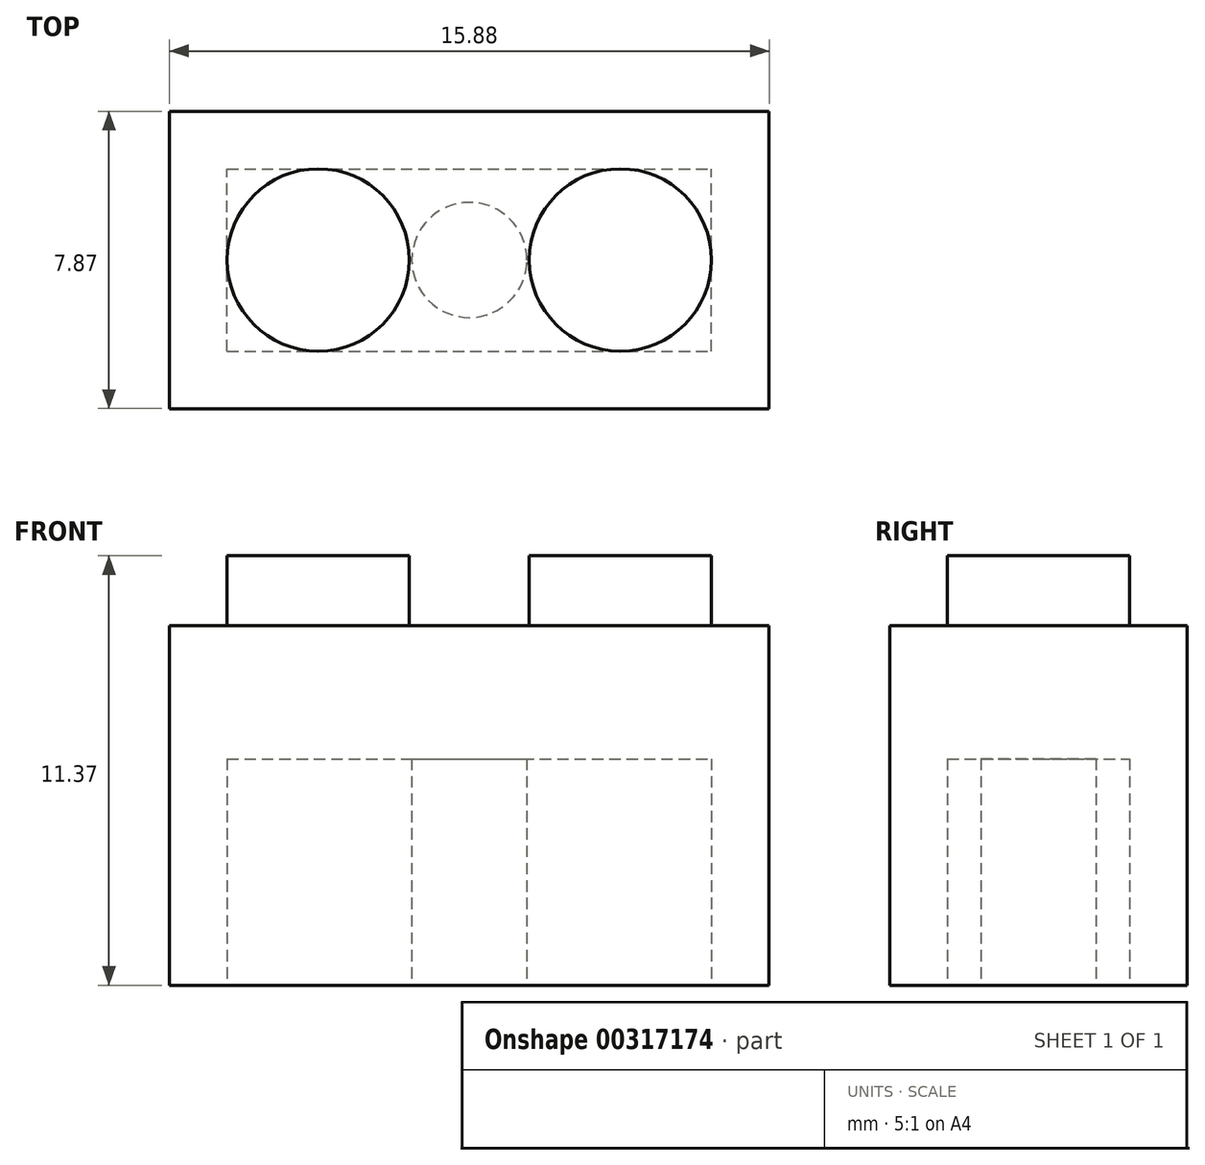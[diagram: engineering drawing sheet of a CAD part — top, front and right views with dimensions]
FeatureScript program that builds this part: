
annotation { "Feature Type Name" : "Feature", "Feature Type Description" : "" }
export const myFeature = defineFeature(function(context is Context, id is Id, definition is map)
    precondition{}
    {
        {
            var Q0;
            Q0=qCreatedBy(makeId("Front.planeOp"),FACE);
            var sketch = newSketch(context, id + "F0", { "sketchPlane" : qUnion([Q0])});
            skLineSegment(sketch, "E0.bottom", {"start": v(-8.22, 8.85) * mm, "end": v(7.66, 8.85) * mm});
            skLineSegment(sketch, "E0.top", {"start": v(-8.22, -0.67) * mm, "end": v(7.66, -0.67) * mm});
            skLineSegment(sketch, "E0.left", {"start": v(-8.22, 8.85) * mm, "end": v(-8.22, -0.67) * mm});
            skLineSegment(sketch, "E0.right", {"start": v(7.66, 8.85) * mm, "end": v(7.66, -0.67) * mm});
            skSolve(sketch);
        }
        {
            var Q0;
            Q0 = qSketchRegion(id + "F0", true);
            extrude(context, id + "F1", {"entities" : qUnion([Q0]), "depth" : 7.87 * mm});
        }
        {
            var Q0;
            Q0=makeQuery(id+"F1.opExtrude","SWEPT_FACE",FACE,{"disambiguationData":[OSD([sQuery(id+"F0.wireOp",EDGE,"E0.bottom")])]});
            var sketch = newSketch(context, id + "F2", { "sketchPlane" : qUnion([Q0])});
            skCircle(sketch, "E1", {"center": v(-4.28, -3.94) * mm, "radius": 2.41 * mm});
            skPoint(sketch, "E1.centerSnap0", {"position": v(7.66, -3.94) * mm});
            skCircle(sketch, "E2", {"center": v(3.72, -3.94) * mm, "radius": 2.41 * mm});
            skSolve(sketch);
        }
        {
            var Q0;
            Q0 = qSketchRegion(id + "F2", true);
            extrude(context, id + "F3", {"entities" : qUnion([Q0]), "operationType" : NewBodyOperationType.ADD, "depth" : 1.85 * mm});
        }
        {
            var Q0;
            Q0=makeQuery(id+"F1.opExtrude","SWEPT_FACE",FACE,{"disambiguationData":[OSD([sQuery(id+"F0.wireOp",EDGE,"E0.top")])]});
            var sketch = newSketch(context, id + "F4", { "sketchPlane" : qUnion([Q0])});
            skPoint(sketch, "E3.centerSnap1", {"position": v(0, 0) * mm});
            skLineSegment(sketch, "E4.bottom", {"start": v(-6.7, 6.35) * mm, "end": v(6.13, 6.35) * mm});
            skLineSegment(sketch, "E4.top", {"start": v(-6.7, 1.52) * mm, "end": v(6.13, 1.52) * mm});
            skLineSegment(sketch, "E4.left", {"start": v(-6.7, 6.35) * mm, "end": v(-6.7, 1.52) * mm});
            skLineSegment(sketch, "E4.right", {"start": v(6.13, 6.35) * mm, "end": v(6.13, 1.52) * mm});
            skCircle(sketch, "E5", {"center": v(-0.28, 3.94) * mm, "radius": 1.52 * mm});
            skPoint(sketch, "E5.centerSnap0", {"position": v(-6.7, 3.94) * mm});
            skPoint(sketch, "E6", {"position": v(-0.28, 6.35) * mm});
            skSolve(sketch);
        }
        {
            var Q0;
            Q0 = qSketchRegion(id + "F4", true);
            extrude(context, id + "F5", {"entities" : qUnion([Q0]), "operationType" : NewBodyOperationType.REMOVE, "oppositeDirection" : true, "depth" : 6 * mm});
        }
    });
